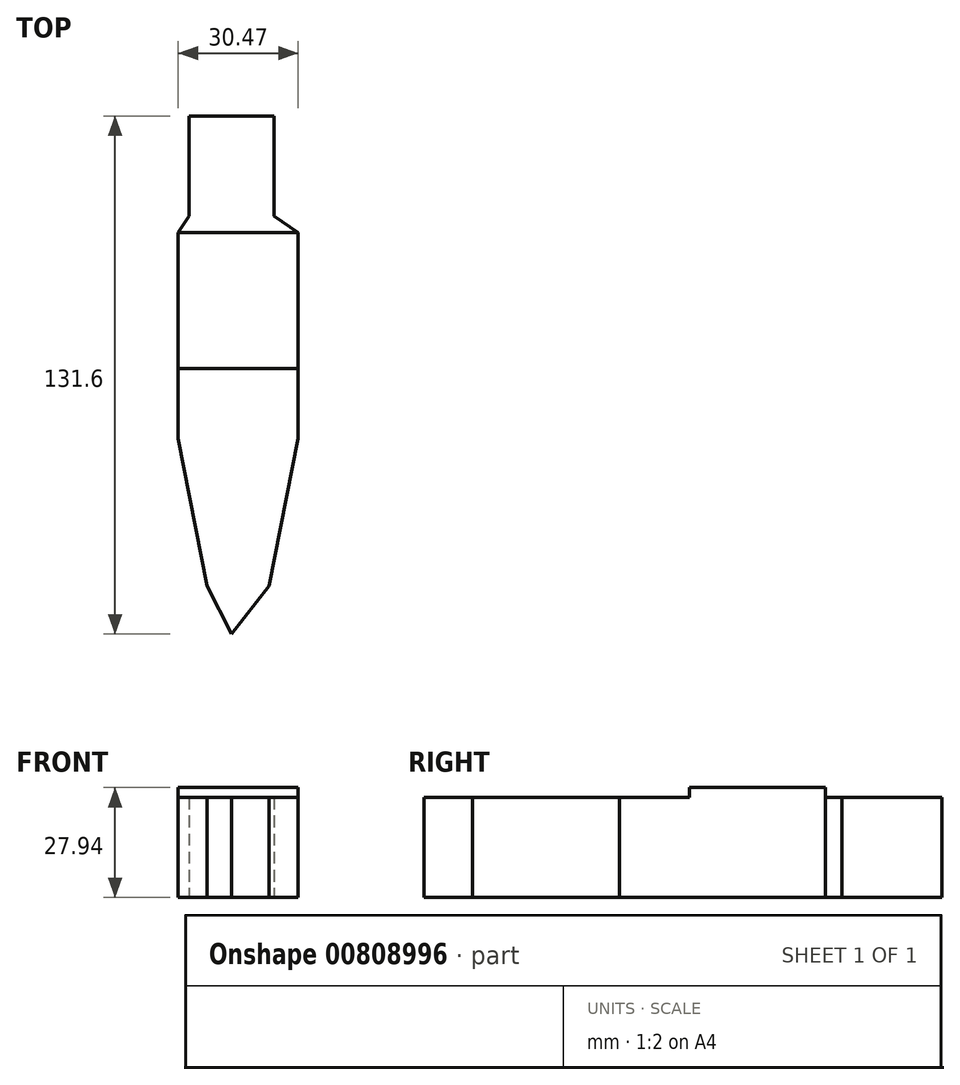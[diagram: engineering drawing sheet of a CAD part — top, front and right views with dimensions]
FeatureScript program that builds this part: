
annotation { "Feature Type Name" : "Feature", "Feature Type Description" : "" }
export const myFeature = defineFeature(function(context is Context, id is Id, definition is map)
    precondition{}
    {
        {
            var Q0;
            Q0=qCreatedBy(makeId("Top.planeOp"),FACE);
            var sketch = newSketch(context, id + "F0", { "sketchPlane" : qUnion([Q0])});
            skLineSegment(sketch, "E0", {"start": v(0, 0) * mm, "end": v(19.05, 0) * mm});
            skLineSegment(sketch, "E1", {"start": v(19.05, 0) * mm, "end": v(100.54, 13.21) * mm});
            skLineSegment(sketch, "E2", {"start": v(100.54, 13.21) * mm, "end": v(100.54, 25.85) * mm});
            skLineSegment(sketch, "E3", {"start": v(100.54, 25.85) * mm, "end": v(25.29, 38.77) * mm});
            skLineSegment(sketch, "E4", {"start": v(25.29, 38.77) * mm, "end": v(0, 38.77) * mm});
            skLineSegment(sketch, "E5", {"start": v(0, 38.77) * mm, "end": v(0, 64.17) * mm});
            skLineSegment(sketch, "E6", {"start": v(0, 64.17) * mm, "end": v(-21.59, 64.17) * mm});
            skLineSegment(sketch, "E7", {"start": v(-21.59, 64.17) * mm, "end": v(-21.59, 38.77) * mm});
            skLineSegment(sketch, "E8", {"start": v(-21.59, 38.77) * mm, "end": v(12.64, 38.77) * mm});
            skLineSegment(sketch, "E9", {"start": v(-21.59, 38.77) * mm, "end": v(-46.89, 38.77) * mm});
            skLineSegment(sketch, "E10", {"start": v(0, 0) * mm, "end": v(-21.59, 0) * mm});
            skLineSegment(sketch, "E11", {"start": v(-21.59, 0) * mm, "end": v(-40.64, 0) * mm});
            skLineSegment(sketch, "E12", {"start": v(-125.9, 11.69) * mm, "end": v(-125.9, 25.85) * mm});
            skLineSegment(sketch, "E13", {"start": v(-125.9, 25.85) * mm, "end": v(-46.89, 38.77) * mm});
            skLineSegment(sketch, "E14", {"start": v(-21.59, 38.77) * mm, "end": v(-24.4, 34.54) * mm});
            skLineSegment(sketch, "E15", {"start": v(-24.4, 34.54) * mm, "end": v(6.07, 34.54) * mm});
            skLineSegment(sketch, "E16", {"start": v(6.07, 34.54) * mm, "end": v(0, 38.77) * mm});
            skLineSegment(sketch, "E17", {"start": v(6.07, 34.54) * mm, "end": v(6.07, 0) * mm});
            skLineSegment(sketch, "E18", {"start": v(6.07, 0) * mm, "end": v(-21.59, 0) * mm});
            skLineSegment(sketch, "E19", {"start": v(-24.4, 34.54) * mm, "end": v(-24.4, 0) * mm});
            skLineSegment(sketch, "E20", {"start": v(-40.64, 0) * mm, "end": v(-125.9, 11.69) * mm});
            skLineSegment(sketch, "E21", {"start": v(-24.4, 0) * mm, "end": v(-24.4, -17.78) * mm});
            skLineSegment(sketch, "E22", {"start": v(6.07, 0) * mm, "end": v(6.07, -17.78) * mm});
            skLineSegment(sketch, "E23", {"start": v(-10.8, 0) * mm, "end": v(-10.8, -50.8) * mm});
            skLineSegment(sketch, "E24", {"start": v(6.07, -17.78) * mm, "end": v(-1.26, -55.17) * mm});
            skLineSegment(sketch, "E25", {"start": v(-24.4, -17.78) * mm, "end": v(-17.08, -55.17) * mm});
            skLineSegment(sketch, "E26", {"start": v(-17.08, -55.17) * mm, "end": v(-10.8, -67.43) * mm});
            skLineSegment(sketch, "E27", {"start": v(-10.8, -67.43) * mm, "end": v(-1.26, -55.17) * mm});
            skLineSegment(sketch, "E28", {"start": v(-1.26, -55.17) * mm, "end": v(29.9, -61.27) * mm});
            skArc(sketch, "E29", {"start": v(34.17, -68.66) * mm, "mid": v(33.71, -64) * mm, "end": v(29.9, -61.27) * mm});
            skLineSegment(sketch, "E30", {"start": v(34.17, -68.66) * mm, "end": v(-10.8, -67.43) * mm});
            skArc(sketch, "E31", {"start": v(25.74, -73.3) * mm, "mid": v(30.7, -72.33) * mm, "end": v(34.17, -68.66) * mm});
            skArc(sketch, "E32", {"start": v(-10.8, -67.43) * mm, "mid": v(6.83, -74.35) * mm, "end": v(25.74, -73.3) * mm});
            skLineSegment(sketch, "E33", {"start": v(-17.08, -55.17) * mm, "end": v(-48.23, -61.27) * mm});
            skArc(sketch, "E34", {"start": v(-48.23, -61.27) * mm, "mid": v(-51.7, -63.47) * mm, "end": v(-52.78, -67.43) * mm});
            skLineSegment(sketch, "E35", {"start": v(-52.78, -67.43) * mm, "end": v(-10.8, -67.43) * mm});
            skArc(sketch, "E36", {"start": v(-52.78, -67.43) * mm, "mid": v(-48.46, -73.05) * mm, "end": v(-41.39, -73.3) * mm});
            skArc(sketch, "E37", {"start": v(-41.39, -73.3) * mm, "mid": v(-25.56, -73.14) * mm, "end": v(-10.8, -67.43) * mm});
            skSolve(sketch);
        }
        {
            var Q0;
            {var subQ0=sQuery(id+"F0.wireOp",EDGE,"E5");Q0=makeQuery(id+"F0.imprint","IMPRINT",FACE,{"disambiguationData":[TD([[makeQuery(id+"F0.imprint","IMPRINT",EDGE,{"derivedFrom":subQ0}),1.0]])]});}
            var Q1;
            {var subQ2=sQuery(id+"F0.wireOp",EDGE,"E14");Q1=makeQuery(id+"F0.imprint","IMPRINT",FACE,{"disambiguationData":[TD([[makeQuery(id+"F0.imprint","IMPRINT",EDGE,{"derivedFrom":subQ2}),1.0]])]});}
            extrude(context, id + "F1", {"entities" : qUnion([Q0, Q1]), "depth" : 25.4 * mm, "offsetDistance" : 25.4 * mm});
        }
        {
            var Q0;
            Q0=makeQuery(id+"F0.imprint","IMPRINT",FACE,{"disambiguationData":[TD([[makeQuery(id+"F0.imprint","IMPRINT",EDGE,{"derivedFrom":sQuery(id+"F0.wireOp",EDGE,"E15")}),-1.0]])]});
            extrude(context, id + "F2", {"entities" : qUnion([Q0]), "operationType" : NewBodyOperationType.ADD, "depth" : 27.94 * mm, "offsetDistance" : 25.4 * mm});
        }
        {
            var Q0;
            {var subQ0=sQuery(id+"F0.wireOp",EDGE,"E21");Q0=makeQuery(id+"F0.imprint","IMPRINT",FACE,{"disambiguationData":[TD([[makeQuery(id+"F0.imprint","IMPRINT",EDGE,{"derivedFrom":subQ0}),1.0]])]});}
            extrude(context, id + "F3", {"entities" : qUnion([Q0]), "operationType" : NewBodyOperationType.ADD, "depth" : 25.4 * mm, "offsetDistance" : 25.4 * mm});
        }
    });
